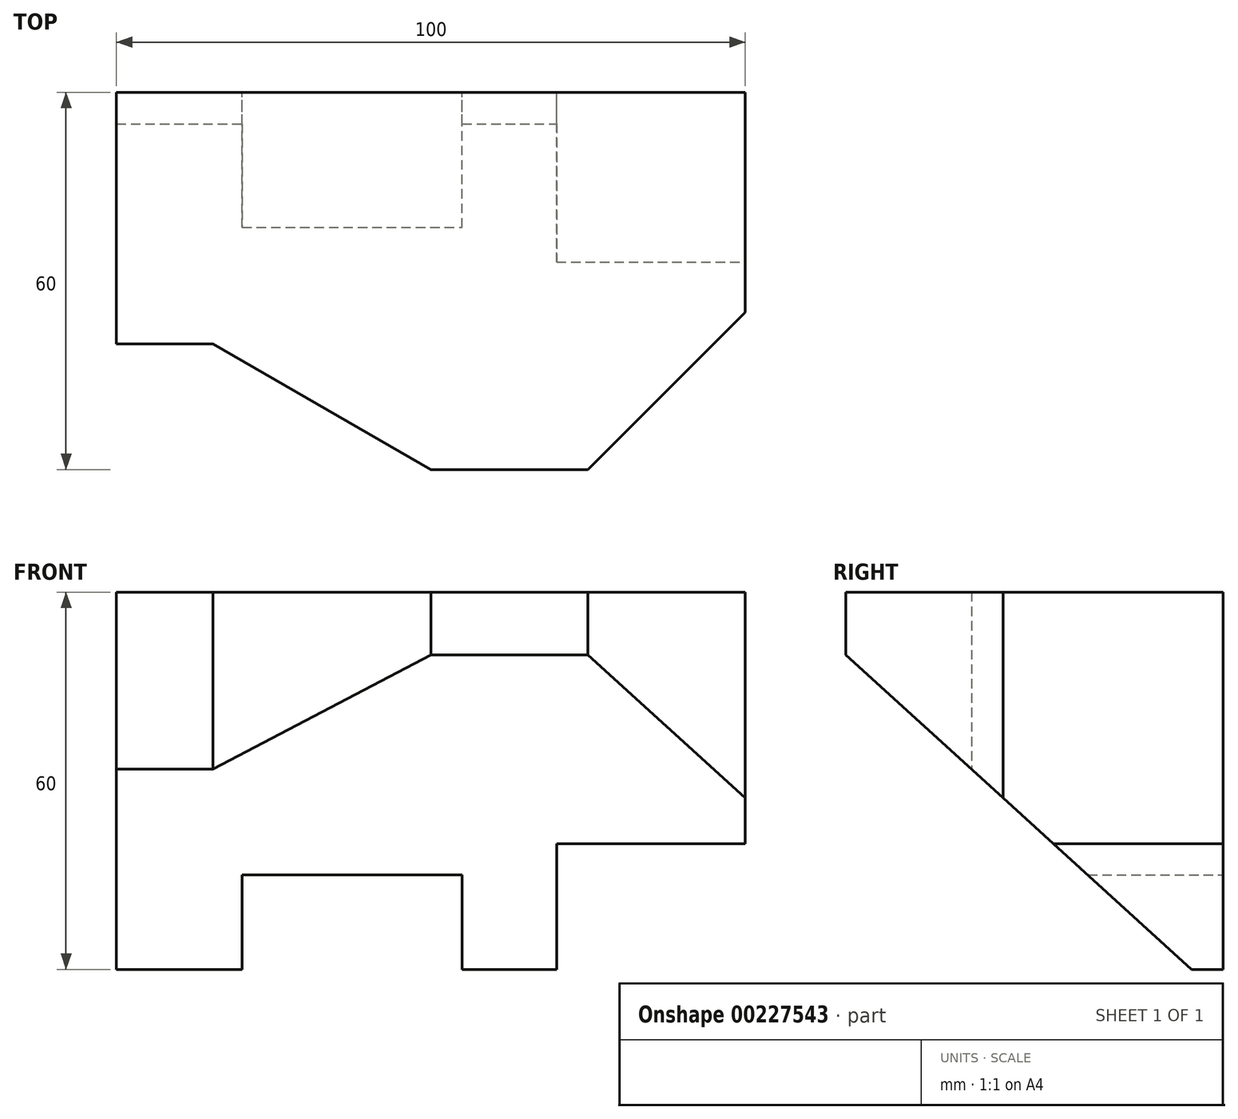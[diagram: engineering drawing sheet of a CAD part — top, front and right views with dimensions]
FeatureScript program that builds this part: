
annotation { "Feature Type Name" : "Feature", "Feature Type Description" : "" }
export const myFeature = defineFeature(function(context is Context, id is Id, definition is map)
    precondition{}
    {
        {
            var Q0;
            Q0=qCreatedBy(makeId("Front.planeOp"),FACE);
            var sketch = newSketch(context, id + "F0", { "sketchPlane" : qUnion([Q0])});
            skLineSegment(sketch, "E0", {"start": v(-31.58, 52.71) * mm, "end": v(68.42, 52.71) * mm});
            skLineSegment(sketch, "E1", {"start": v(68.42, 52.71) * mm, "end": v(68.42, 12.71) * mm});
            skLineSegment(sketch, "E2", {"start": v(68.42, 12.71) * mm, "end": v(38.42, 12.71) * mm});
            skLineSegment(sketch, "E3", {"start": v(38.42, 12.71) * mm, "end": v(38.42, -7.29) * mm});
            skLineSegment(sketch, "E4", {"start": v(38.42, -7.29) * mm, "end": v(23.42, -7.29) * mm});
            skLineSegment(sketch, "E5", {"start": v(23.42, -7.29) * mm, "end": v(23.42, 7.71) * mm});
            skLineSegment(sketch, "E6", {"start": v(23.42, 7.71) * mm, "end": v(-11.58, 7.71) * mm});
            skLineSegment(sketch, "E7", {"start": v(-11.58, 7.71) * mm, "end": v(-11.58, -7.29) * mm});
            skLineSegment(sketch, "E8", {"start": v(-11.58, -7.29) * mm, "end": v(-31.58, -7.29) * mm});
            skLineSegment(sketch, "E9", {"start": v(-31.58, -7.29) * mm, "end": v(-31.58, 52.71) * mm});
            skSolve(sketch);
        }
        {
            var Q0;
            Q0 = qSketchRegion(id + "F0", true);
            extrude(context, id + "F1", {"entities" : qUnion([Q0]), "depth" : 60 * mm});
        }
        {
            var Q0;
            Q0=makeQuery(id+"F1.opExtrude","SWEPT_FACE",FACE,{"disambiguationData":[OSD([sQuery(id+"F0.wireOp",EDGE,"E8")])]});
            var sketch = newSketch(context, id + "F2", { "sketchPlane" : qUnion([Q0])});
            skLineSegment(sketch, "E10.0.0", {"start": v(-31.58, 0) * mm, "end": v(-11.58, 0) * mm, "construction": true});
            skLineSegment(sketch, "E10.0.1", {"start": v(-11.58, 0) * mm, "end": v(-11.58, 60) * mm, "construction": true});
            skLineSegment(sketch, "E10.0.2", {"start": v(-11.58, 60) * mm, "end": v(-31.58, 60) * mm, "construction": true});
            skLineSegment(sketch, "E10.0.3", {"start": v(-31.58, 60) * mm, "end": v(-31.58, 0) * mm, "construction": true});
            skLineSegment(sketch, "E11.0.0", {"start": v(-11.58, 0) * mm, "end": v(23.42, 0) * mm, "construction": true});
            skLineSegment(sketch, "E11.0.1", {"start": v(23.42, 0) * mm, "end": v(23.42, 60) * mm, "construction": true});
            skLineSegment(sketch, "E11.0.2", {"start": v(23.42, 60) * mm, "end": v(-11.58, 60) * mm, "construction": true});
            skLineSegment(sketch, "E11.0.3", {"start": v(-11.58, 60) * mm, "end": v(-11.58, 0) * mm, "construction": true});
            skLineSegment(sketch, "E12.0.0", {"start": v(23.42, 0) * mm, "end": v(38.42, 0) * mm, "construction": true});
            skLineSegment(sketch, "E12.0.1", {"start": v(38.42, 0) * mm, "end": v(38.42, 60) * mm, "construction": true});
            skLineSegment(sketch, "E12.0.2", {"start": v(38.42, 60) * mm, "end": v(23.42, 60) * mm, "construction": true});
            skLineSegment(sketch, "E12.0.3", {"start": v(23.42, 60) * mm, "end": v(23.42, 0) * mm, "construction": true});
            skLineSegment(sketch, "E13.0.0", {"start": v(38.42, 0) * mm, "end": v(68.42, 0) * mm, "construction": true});
            skLineSegment(sketch, "E13.0.1", {"start": v(68.42, 0) * mm, "end": v(68.42, 60) * mm, "construction": true});
            skLineSegment(sketch, "E13.0.2", {"start": v(68.42, 60) * mm, "end": v(38.42, 60) * mm, "construction": true});
            skLineSegment(sketch, "E13.0.3", {"start": v(38.42, 60) * mm, "end": v(38.42, 0) * mm, "construction": true});
            skLineSegment(sketch, "E14", {"start": v(43.42, 60) * mm, "end": v(68.42, 60) * mm});
            skLineSegment(sketch, "E15", {"start": v(68.42, 35) * mm, "end": v(43.42, 60) * mm});
            skLineSegment(sketch, "E16", {"start": v(-31.58, 60) * mm, "end": v(18.42, 60) * mm});
            skLineSegment(sketch, "E17", {"start": v(18.42, 60) * mm, "end": v(-16.22, 40) * mm});
            skLineSegment(sketch, "E18", {"start": v(-16.22, 40) * mm, "end": v(-31.58, 40) * mm});
            skLineSegment(sketch, "E19", {"start": v(-31.58, 40) * mm, "end": v(-31.58, 60) * mm});
            skLineSegment(sketch, "E20", {"start": v(68.42, 60) * mm, "end": v(68.42, 35) * mm});
            skSolve(sketch);
        }
        {
            var Q0;
            Q0 = qSketchRegion(id + "F2", true);
            extrude(context, id + "F3", {"entities" : qUnion([Q0]), "operationType" : NewBodyOperationType.REMOVE, "endBound" : BoundingType.THROUGH_ALL, "oppositeDirection" : true, "depth" : 25 * mm});
        }
        {
            var Q0;
            Q0=makeQuery(id+"F1.opExtrude","SWEPT_FACE",FACE,{"disambiguationData":[OSD([sQuery(id+"F0.wireOp",EDGE,"E1")])]});
            var sketch = newSketch(context, id + "F4", { "sketchPlane" : qUnion([Q0])});
            skLineSegment(sketch, "E21.0.0", {"start": v(0, -7.29) * mm, "end": v(0, 12.71) * mm, "construction": true});
            skLineSegment(sketch, "E21.0.1", {"start": v(0, 12.71) * mm, "end": v(-60, 12.71) * mm, "construction": true});
            skLineSegment(sketch, "E21.0.2", {"start": v(-60, 12.71) * mm, "end": v(-60, -7.29) * mm, "construction": true});
            skLineSegment(sketch, "E21.0.3", {"start": v(-60, -7.29) * mm, "end": v(0, -7.29) * mm, "construction": true});
            skLineSegment(sketch, "E22.0.0", {"start": v(-35, 12.71) * mm, "end": v(-35, 52.71) * mm, "construction": true});
            skLineSegment(sketch, "E22.0.1", {"start": v(-35, 52.71) * mm, "end": v(-60, 52.71) * mm, "construction": true});
            skLineSegment(sketch, "E22.0.2", {"start": v(-60, 52.71) * mm, "end": v(-60, 12.71) * mm, "construction": true});
            skLineSegment(sketch, "E22.0.3", {"start": v(-60, 12.71) * mm, "end": v(-35, 12.71) * mm, "construction": true});
            skLineSegment(sketch, "E23.0.0", {"start": v(0, 52.71) * mm, "end": v(-35, 52.71) * mm, "construction": true});
            skLineSegment(sketch, "E23.0.1", {"start": v(-35, 52.71) * mm, "end": v(-35, 12.71) * mm, "construction": true});
            skLineSegment(sketch, "E23.0.2", {"start": v(-35, 12.71) * mm, "end": v(0, 12.71) * mm, "construction": true});
            skLineSegment(sketch, "E23.0.3", {"start": v(0, 12.71) * mm, "end": v(0, 52.71) * mm, "construction": true});
            skLineSegment(sketch, "E24", {"start": v(-60, -7.29) * mm, "end": v(-5, -7.29) * mm});
            skLineSegment(sketch, "E25", {"start": v(-5, -7.29) * mm, "end": v(-60, 42.71) * mm});
            skLineSegment(sketch, "E26", {"start": v(-60, 42.71) * mm, "end": v(-60, -7.29) * mm});
            skSolve(sketch);
        }
        {
            var Q0;
            {var subQ4=sQuery(id+"F4.wireOp",EDGE,"E24");Q0=makeQuery(id+"F4.imprint","IMPRINT",FACE,{"disambiguationData":[TD([[makeQuery(id+"F4.imprint","IMPRINT",EDGE,{"derivedFrom":subQ4}),1.0]])]});}
            var Q1;
            {var subQ0=sQuery(id+"F4.wireOp",EDGE,"E25");var subQ1=makeQuery(id+"F1.opExtrude","SWEPT_EDGE",EDGE,{"disambiguationData":[OSD([sQuery(id+"F0.wireOp",EDGE,"E1"),sQuery(id+"F0.wireOp",EDGE,"E2")])]});var subQ2=makeQuery(id+"F4.imprint","INTERSECT",VERTEX,{"derivedFrom":[subQ1,subQ0]});Q1=makeQuery(id+"F4.imprint","IMPRINT",FACE,{"disambiguationData":[TD([[makeQuery(id+"F4.imprint","IMPRINT",EDGE,{"disambiguationData":[TD([[subQ2,-1.0]])],"derivedFrom":subQ0}),1.0]])]});}
            extrude(context, id + "F5", {"entities" : qUnion([Q0, Q1]), "operationType" : NewBodyOperationType.REMOVE, "endBound" : BoundingType.THROUGH_ALL, "oppositeDirection" : true, "depth" : 25 * mm});
        }
    });
